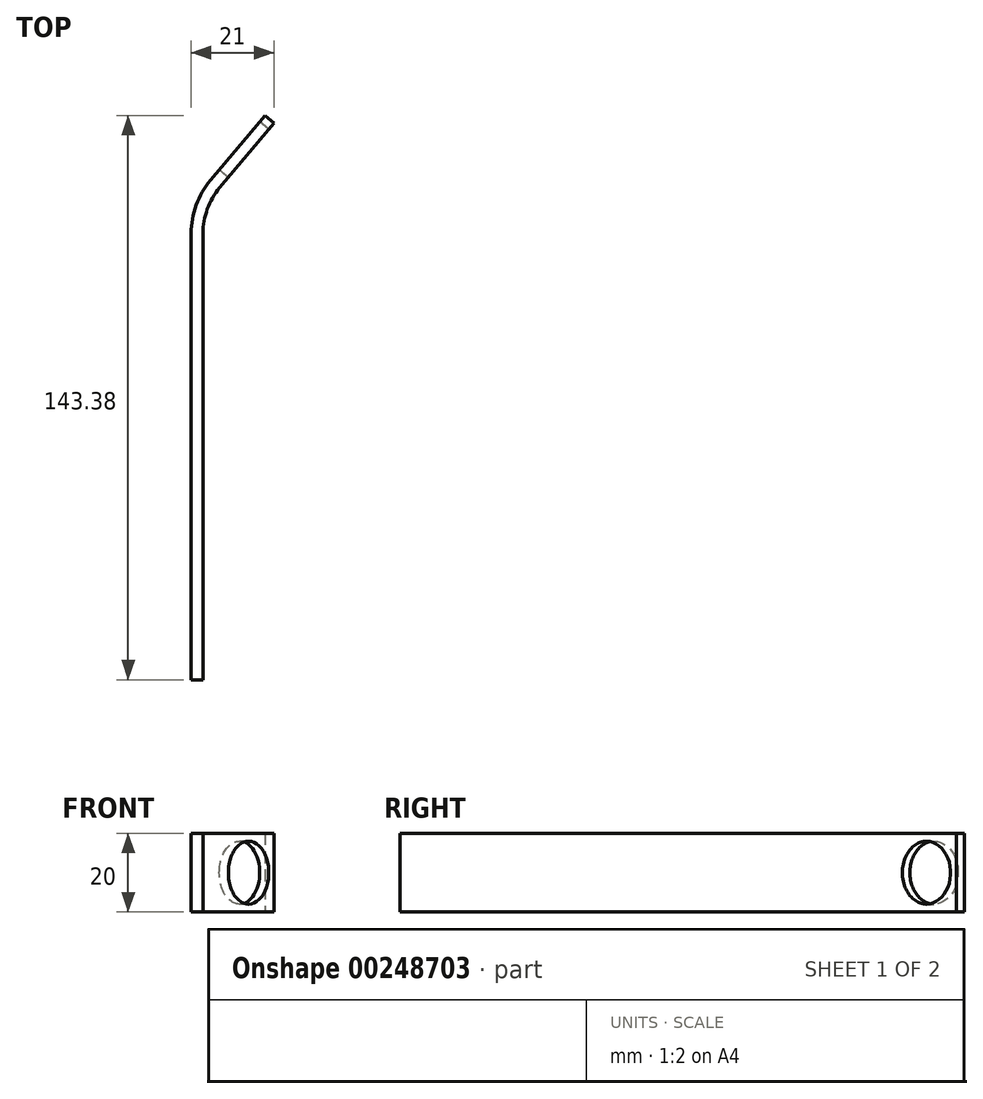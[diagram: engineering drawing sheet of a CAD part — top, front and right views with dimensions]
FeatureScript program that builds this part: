
annotation { "Feature Type Name" : "Feature", "Feature Type Description" : "" }
export const myFeature = defineFeature(function(context is Context, id is Id, definition is map)
    precondition{}
    {
        {
            var Q0;
            Q0=qCreatedBy(makeId("Top.planeOp"),FACE);
            var sketch = newSketch(context, id + "F0", { "sketchPlane" : qUnion([Q0])});
            skLineSegment(sketch, "E0", {"start": v(0, 0) * mm, "end": v(0, 113.45) * mm});
            skLineSegment(sketch, "E1", {"start": v(4.21, 125.02) * mm, "end": v(18, 141.45) * mm});
            skPoint(sketch, "E2.visualSharp", {"position": v(0, 120) * mm});
            skArc(sketch, "E2.filletArc", {"start": v(4.21, 125.02) * mm, "mid": v(1.09, 119.6) * mm, "end": v(0, 113.45) * mm});
            skLineSegment(sketch, "E3.0", {"start": v(1.91, 126.95) * mm, "end": v(15.7, 143.38) * mm});
            skArc(sketch, "E3.1", {"start": v(1.91, 126.95) * mm, "mid": v(-1.73, 120.63) * mm, "end": v(-3, 113.45) * mm});
            skLineSegment(sketch, "E3.2", {"start": v(-3, 0) * mm, "end": v(-3, 113.45) * mm});
            skLineSegment(sketch, "E4", {"start": v(15.7, 143.38) * mm, "end": v(18, 141.45) * mm});
            skLineSegment(sketch, "E5", {"start": v(-3, 0) * mm, "end": v(0, 0) * mm});
            skSolve(sketch);
        }
        {
            var Q0;
            Q0 = qSketchRegion(id + "F0", true);
            extrude(context, id + "F1", {"entities" : qUnion([Q0]), "depth" : 20 * mm});
        }
        {
            var Q0;
            Q0=makeQuery(id+"F1.opExtrude","SWEPT_FACE",FACE,{"disambiguationData":[OSD([sQuery(id+"F0.wireOp",EDGE,"E3.0")])]});
            var sketch = newSketch(context, id + "F2", { "sketchPlane" : qUnion([Q0])});
            skCircle(sketch, "E6", {"center": v(-109.93, 10) * mm, "radius": 8 * mm});
            skPoint(sketch, "E6.centerSnap0", {"position": v(-119.93, 10) * mm});
            skSolve(sketch);
        }
        {
            var Q0;
            Q0 = qSketchRegion(id + "F2", true);
            extrude(context, id + "F3", {"entities" : qUnion([Q0]), "operationType" : NewBodyOperationType.REMOVE, "oppositeDirection" : true, "depth" : 4 * mm});
        }
    });
